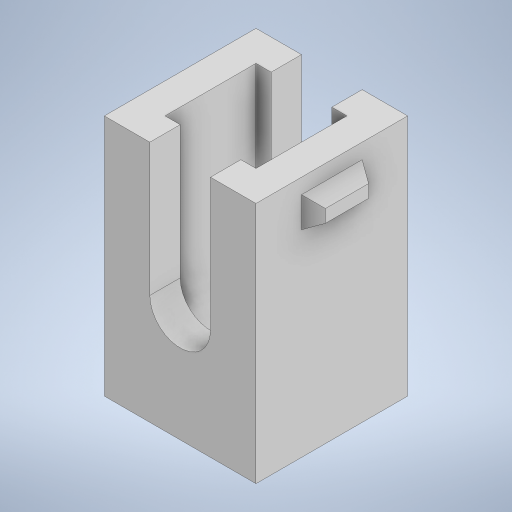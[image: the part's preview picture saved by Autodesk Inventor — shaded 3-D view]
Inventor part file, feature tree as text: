
AUTODESK INVENTOR PART (.ipt)
format: ipt  version: 2023 (Build 270158000, 158)  size: 256,000 bytes
history: native  units: in
note: dims shown in document units (in); Inventor stores cm internally (conversion verified against a paired STEP export)
features: extrude x5, sketch x5, shell x1
ambient origin geometry x8: Origin, YZ Plane, XZ Plane, XY Plane, X Axis, Y Axis, Z Axis, Center Point
bodies: Solid1 (feature_tree)
feature tree (11):
  extrude  "Extrusion1"  Depth=0.1969in
  shell  "Shell1"  Thickness=0.315in
  extrude  "Extrusion4"  Depth=0.0394in
  extrude  "Extrusion5"  Depth=0.0394in
  extrude  "Extrusion6"  Depth=0.0394in
  extrude  "Extrusion7"  Depth=0.0394in
  sketch  "Sketch1"  dims[d0=0.1969in d1=0.1969in d2=0.315in d3=0.0in]
  sketch  "Sketch9"  dims[d4=0.0394in d10=0.0394in]
  sketch  "Sketch10"  dims[d11=0.0197in d12=-0.2061in d13=0.0394in]
  sketch  "Sketch11"  dims[d14=0.0787in d15=0.0394in]
  sketch  "Sketch12"  dims[d16=0.0787in d17=0.0394in d18=0.0197in d19=-0.2061in d20=0.0787in d21=0.0in d22=0.0in d23=0.0787in d24=0.0in d25=0.0in]
